# Revit family: Cabinet-Hardware_L-Shaped-Pull
name_source: partatom
category: Casework
units: mm (PartAtom-declared; Revit-internal decimal feet)

## family parameters
Classification Number = 23.40.35.11.11
Cut with Voids When Loaded = No
Host = Face
Room Calculation Point = No
Shared = Yes

## types (2) — shared parameters
Assembly Code = E2010200
Construction Details = http://www.arcat.com
Default Elevation = 4' - 0"
Door Slab Thickness = 0' - 0 1/2"
Fastener Material = ARCAT - Metal - Steel - ASTM A992
Fastener Type = #8 Phillips Pan Head Machine Screw - Length by door thickness
Green Building-LEED = http://www.arcat.com
Hardware Finish = ARCAT - Metal - Brass, Polished
Hardware Finish Accent = ARCAT - Metal - Bronze, Oil Rubbed
Hole Size = 0' - 0 3/16"
Hole Spacing = 0' - 0"
Keynote = 12300
Manufacturer = Generic
Manufacturer Fax = (203) 929-2444
Manufacturer Website = http://www.arcat.com
Model = Generic
Product Data = http://www.arcat.com
Product Properties = http://www.arcat.com
Specification = http://www.arcat.com
screw_location = 0' - 0"
zero-valued in all types: Expected Lifespan (Years), Maintenance Schedule (Months), Warranty Duration (Years)

## per-type parameters (varying)
| type | Description | Handle Width | screw_offset |
| Drawer-Pull | Drawer / Door Pull -L-Shaped | 0' - 1 1/2" | 0' - 0 1/2" |
| Handle | Drawer / Door Handle | 0' - 2" | 0' - 0" |

## geometry (parser evidence)
native form markers: Sweep x5
no freeform markers — native parametric forms only
